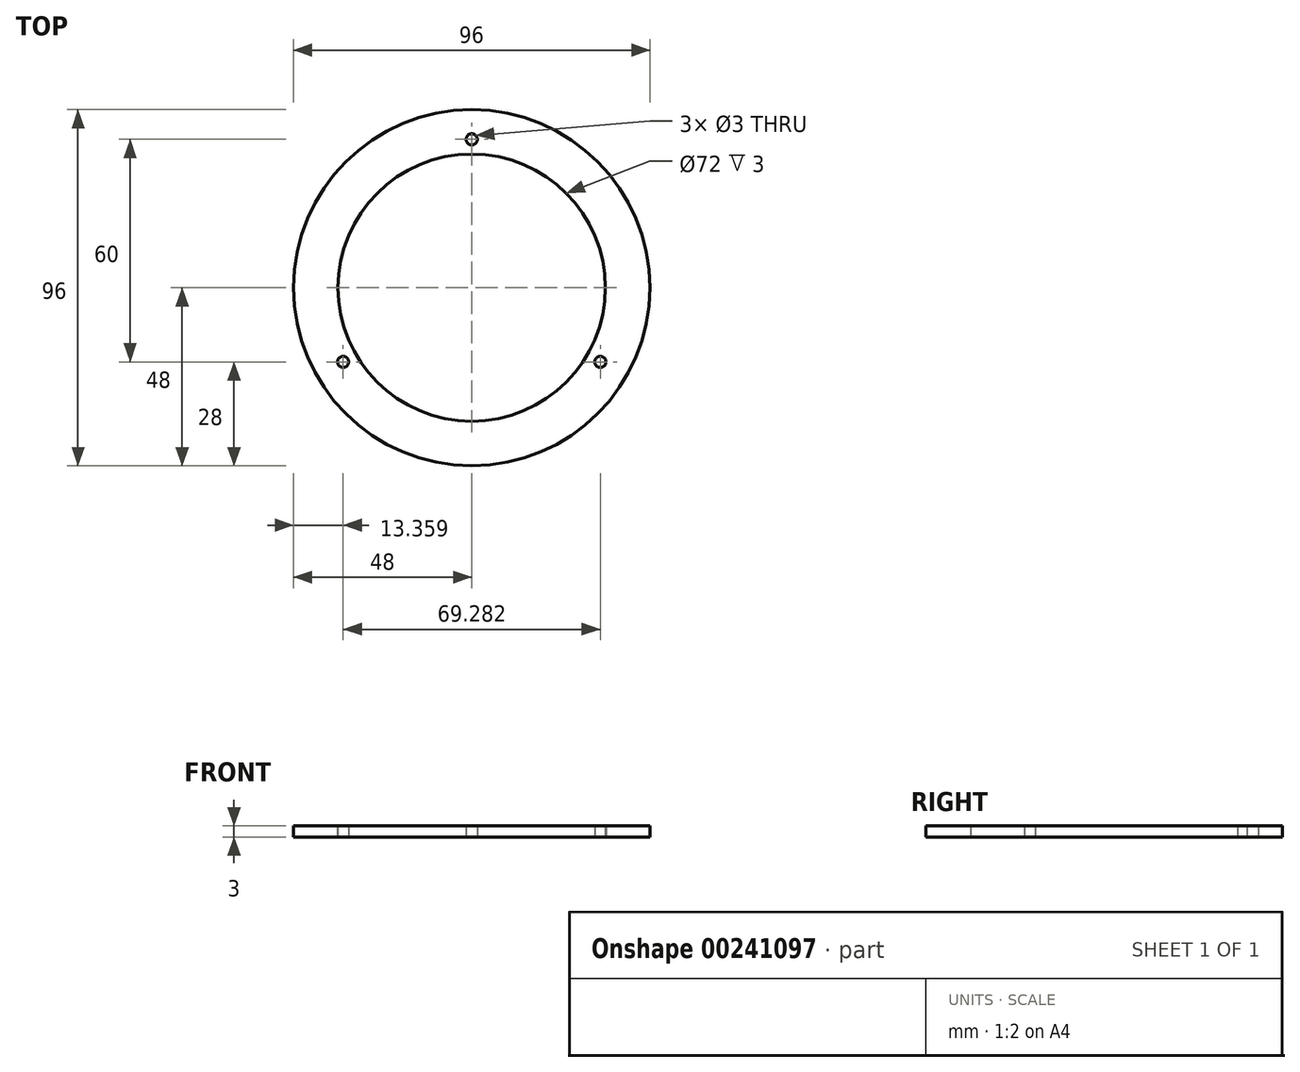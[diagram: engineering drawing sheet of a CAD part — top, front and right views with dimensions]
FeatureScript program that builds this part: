
annotation { "Feature Type Name" : "Feature", "Feature Type Description" : "" }
export const myFeature = defineFeature(function(context is Context, id is Id, definition is map)
    precondition{}
    {
        {
            var Q0;
            Q0=qCreatedBy(makeId("Top.planeOp"),FACE);
            var sketch = newSketch(context, id + "F0", { "sketchPlane" : qUnion([Q0])});
            skCircle(sketch, "E0", {"center": v(0, 0) * mm, "radius": 48 * mm});
            skCircle(sketch, "E1", {"center": v(0, 0) * mm, "radius": 36 * mm});
            skCircle(sketch, "E2", {"center": v(0, 40) * mm, "radius": 1.5 * mm});
            skCircle(sketch, "E3.1.0", {"center": v(-34.64, -20) * mm, "radius": 1.5 * mm});
            skCircle(sketch, "E3.2.0", {"center": v(34.64, -20) * mm, "radius": 1.5 * mm});
            skSolve(sketch);
        }
        {
            var Q0;
            Q0=qSketchRegion(id+"F0",true);
            extrude(context, id + "F1", {"entities" : qUnion([Q0]), "depth" : 3 * mm});
        }
    });
